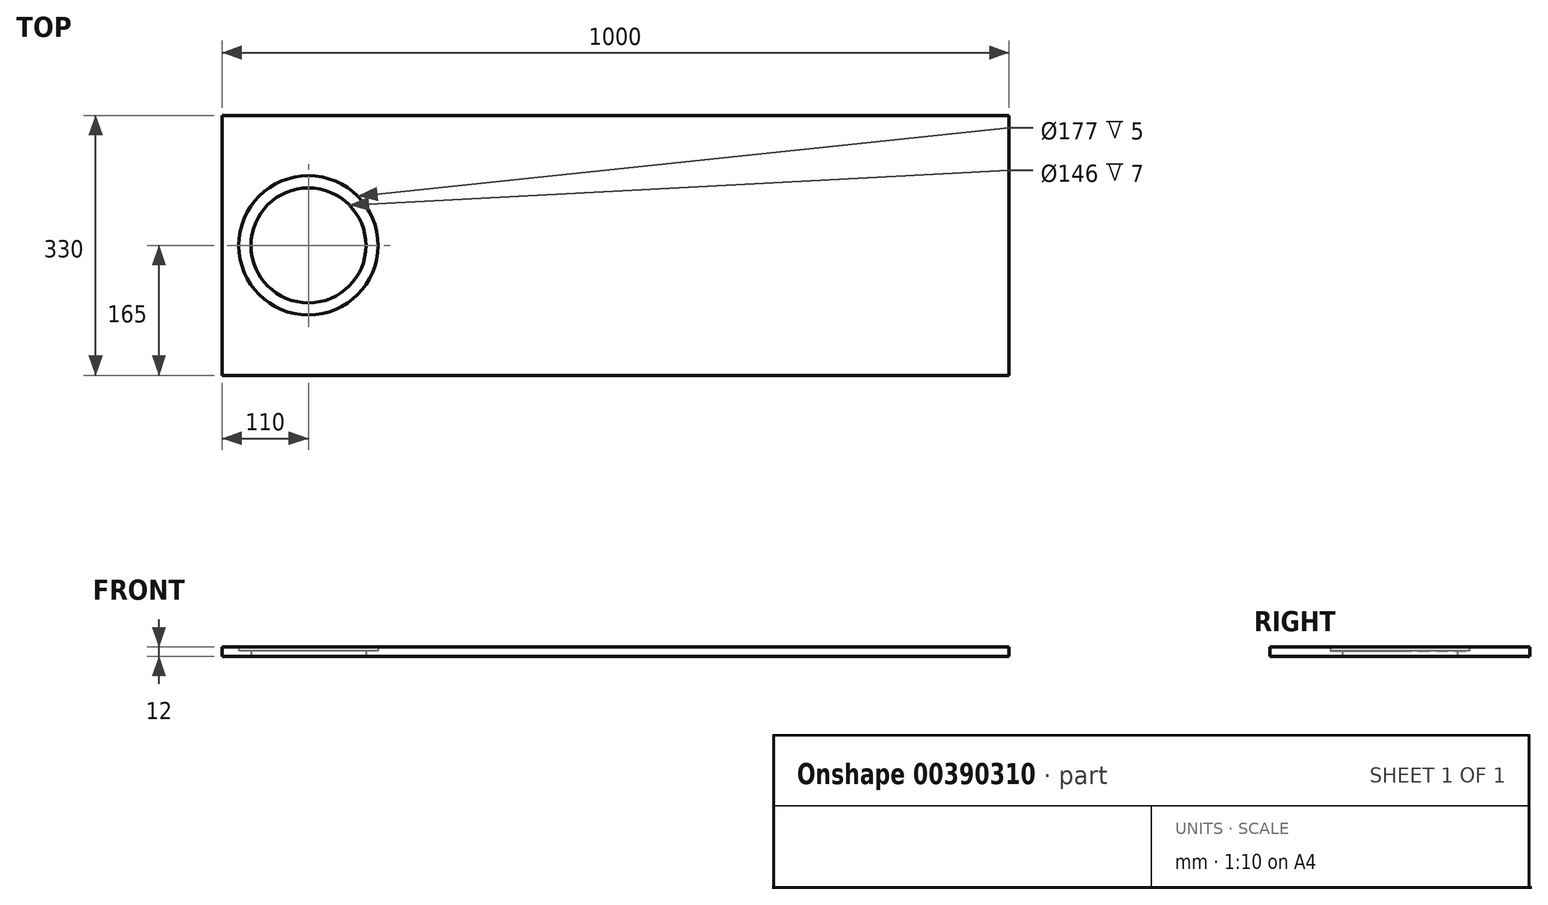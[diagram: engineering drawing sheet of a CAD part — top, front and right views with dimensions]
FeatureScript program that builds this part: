
annotation { "Feature Type Name" : "Feature", "Feature Type Description" : "" }
export const myFeature = defineFeature(function(context is Context, id is Id, definition is map)
    precondition{}
    {
        {
            var Q0;
            Q0=qCreatedBy(makeId("Top.planeOp"),FACE);
            var sketch = newSketch(context, id + "F0", { "sketchPlane" : qUnion([Q0])});
            skLineSegment(sketch, "E0.bottom", {"start": v(0, 0) * mm, "end": v(1000, 0) * mm});
            skLineSegment(sketch, "E0.top", {"start": v(0, 330) * mm, "end": v(1000, 330) * mm});
            skLineSegment(sketch, "E0.left", {"start": v(0, 0) * mm, "end": v(0, 330) * mm});
            skLineSegment(sketch, "E0.right", {"start": v(1000, 0) * mm, "end": v(1000, 330) * mm});
            skCircle(sketch, "E1", {"center": v(110, 165) * mm, "radius": 88.5 * mm});
            skCircle(sketch, "E2", {"center": v(110, 165) * mm, "radius": 73 * mm});
            skSolve(sketch);
        }
        {
            var Q0;
            Q0=makeQuery(id+"F0.imprint","IMPRINT",FACE,{"disambiguationData":[TD([[makeQuery(id+"F0.imprint","IMPRINT",EDGE,{"derivedFrom":sQuery(id+"F0.wireOp",EDGE,"E0.bottom")}),1.0]])]});
            extrude(context, id + "F1", {"entities" : qUnion([Q0]), "depth" : 12 * mm});
        }
        {
            var Q0;
            Q0=makeQuery(id+"F0.imprint","IMPRINT",FACE,{"disambiguationData":[TD([[makeQuery(id+"F0.imprint","IMPRINT",EDGE,{"derivedFrom":sQuery(id+"F0.wireOp",EDGE,"E1")}),1.0]])]});
            extrude(context, id + "F2", {"entities" : qUnion([Q0]), "operationType" : NewBodyOperationType.ADD, "depth" : 7 * mm});
        }
    });
